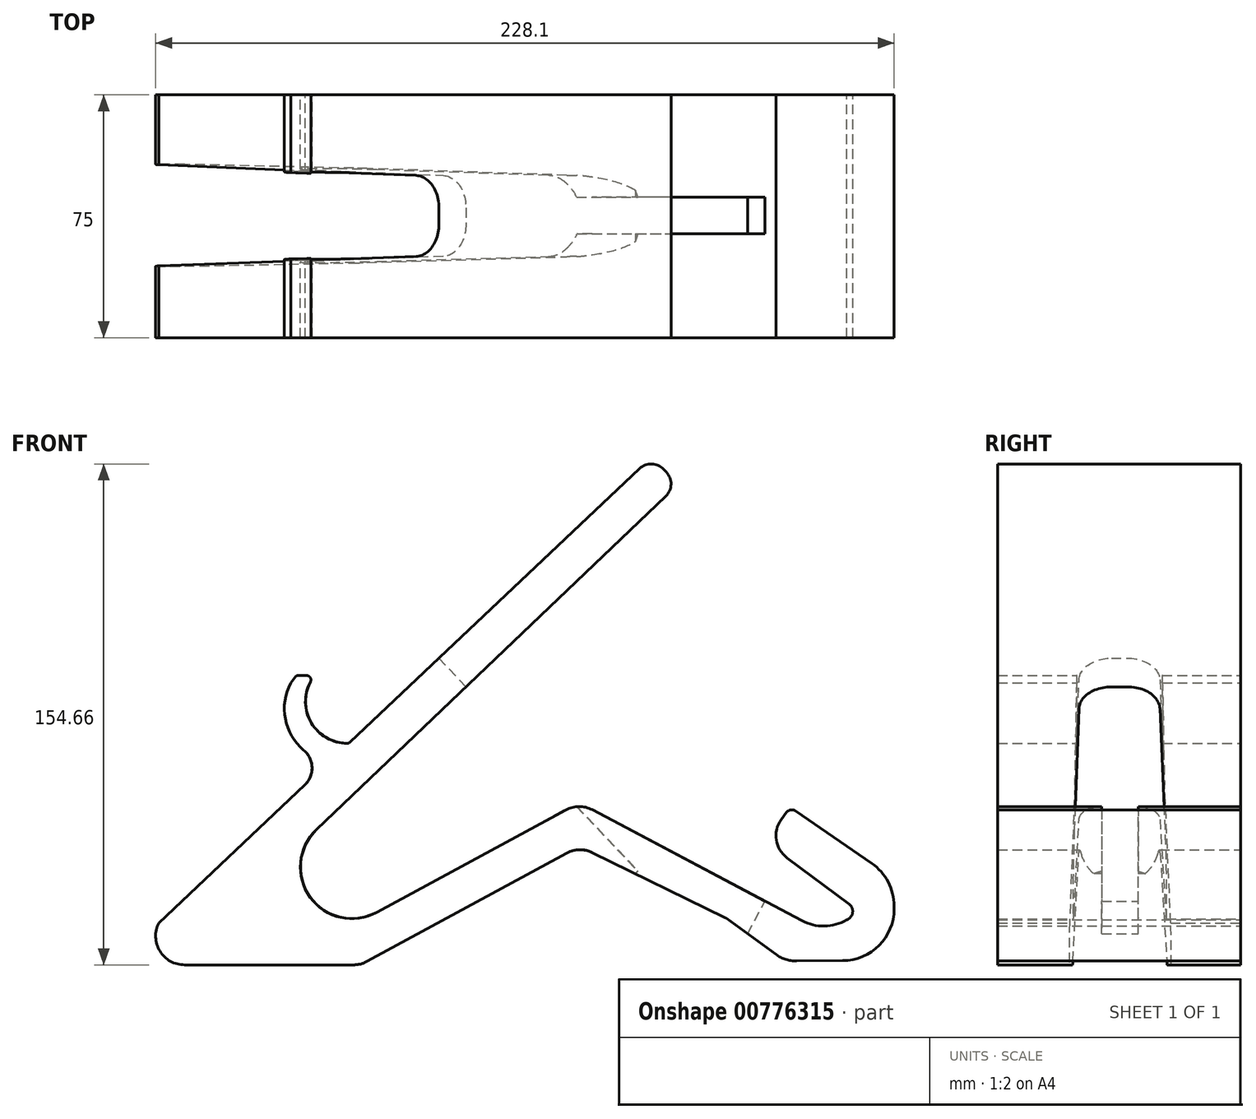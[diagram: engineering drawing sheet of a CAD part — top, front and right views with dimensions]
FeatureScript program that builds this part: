
annotation { "Feature Type Name" : "Feature", "Feature Type Description" : "" }
export const myFeature = defineFeature(function(context is Context, id is Id, definition is map)
    precondition{}
    {
        {
            var Q0;
            Q0=qCreatedBy(makeId("Front.planeOp"),FACE);
            var sketch = newSketch(context, id + "F0", { "sketchPlane" : qUnion([Q0])});
            skLineSegment(sketch, "E0", {"start": v(-57.51, -6.76) * mm, "end": v(31.9, 77.7) * mm});
            skArc(sketch, "E1", {"start": v(-116.6, -62.56) * mm, "mid": v(-116.26, -71.3) * mm, "end": v(-108.62, -75.53) * mm});
            skPoint(sketch, "E2", {"position": v(-116.6, -62.56) * mm});
            skArc(sketch, "E3", {"start": v(-75.86, 11.52) * mm, "mid": v(-77.5, 0.43) * mm, "end": v(-71.82, -9.23) * mm});
            skPoint(sketch, "E4", {"position": v(-54.93, -4.33) * mm});
            skArc(sketch, "E5", {"start": v(-69.78, 11.9) * mm, "mid": v(-69.49, -0.84) * mm, "end": v(-58.4, -7.12) * mm});
            skLineSegment(sketch, "E6", {"start": v(-70.91, 13.8) * mm, "end": v(-73.69, 13.8) * mm});
            skLineSegment(sketch, "E7", {"start": v(-74.26, 13.52) * mm, "end": v(-75.86, 11.52) * mm});
            skPoint(sketch, "E8", {"position": v(-57.87, -7.1) * mm});
            skArc(sketch, "E9.filletArc", {"start": v(-69.78, 11.9) * mm, "mid": v(-69.8, 13.17) * mm, "end": v(-70.91, 13.8) * mm});
            skArc(sketch, "E10.filletArc", {"start": v(-73.69, 13.8) * mm, "mid": v(-74, 13.73) * mm, "end": v(-74.26, 13.52) * mm});
            skArc(sketch, "E11.filletArc", {"start": v(-58.4, -7.12) * mm, "mid": v(-57.92, -7.02) * mm, "end": v(-57.51, -6.76) * mm});
            skLineSegment(sketch, "E12", {"start": v(39.99, 69.19) * mm, "end": v(-67.93, -33.77) * mm});
            skLineSegment(sketch, "E13", {"start": v(-71.52, -19.99) * mm, "end": v(-116.6, -62.56) * mm});
            skLineSegment(sketch, "E14", {"start": v(-49.28, -59.37) * mm, "end": v(9.15, -27.67) * mm});
            skLineSegment(sketch, "E15", {"start": v(17.28, -40.85) * mm, "end": v(58.34, -60.96) * mm});
            skLineSegment(sketch, "E16", {"start": v(58.65, -61.14) * mm, "end": v(74.02, -72.3) * mm});
            skArc(sketch, "E17.filletArc", {"start": v(-67.93, -33.77) * mm, "mid": v(-69.82, -54.73) * mm, "end": v(-49.28, -59.37) * mm});
            skPoint(sketch, "E18.visualSharp", {"position": v(110.3, -50.19) * mm});
            skArc(sketch, "E19.filletArc", {"start": v(-71.52, -19.99) * mm, "mid": v(-69.26, -14.54) * mm, "end": v(-71.82, -9.23) * mm});
            skLineSegment(sketch, "E20", {"start": v(84, -74.31) * mm, "end": v(94.64, -74.24) * mm});
            skLineSegment(sketch, "E21", {"start": v(110.52, -58.27) * mm, "end": v(110.52, -57.36) * mm});
            skLineSegment(sketch, "E22", {"start": v(103.6, -44.2) * mm, "end": v(80.06, -28.02) * mm});
            skArc(sketch, "E23.filletArc", {"start": v(74.02, -72.3) * mm, "mid": v(77.02, -73.82) * mm, "end": v(80.35, -74.33) * mm});
            skArc(sketch, "E24.filletArc", {"start": v(94.64, -74.24) * mm, "mid": v(105.87, -69.53) * mm, "end": v(110.52, -58.27) * mm});
            skPoint(sketch, "E25.visualSharp", {"position": v(110.52, -48.96) * mm});
            skArc(sketch, "E25.filletArc", {"start": v(110.52, -57.36) * mm, "mid": v(108.68, -49.92) * mm, "end": v(103.6, -44.2) * mm});
            skLineSegment(sketch, "E26", {"start": v(80.35, -74.33) * mm, "end": v(84, -74.31) * mm});
            skLineSegment(sketch, "E27", {"start": v(-108.62, -75.53) * mm, "end": v(-56.4, -75.53) * mm});
            skLineSegment(sketch, "E28", {"start": v(-52.3, -74.5) * mm, "end": v(9.4, -41.02) * mm});
            skPoint(sketch, "E29.visualSharp", {"position": v(-54.22, -75.53) * mm});
            skArc(sketch, "E29.filletArc", {"start": v(-56.4, -75.53) * mm, "mid": v(-54.29, -75.27) * mm, "end": v(-52.3, -74.5) * mm});
            skLineSegment(sketch, "E30", {"start": v(17.27, -27.63) * mm, "end": v(81.99, -61.9) * mm});
            skArc(sketch, "E31.filletArc", {"start": v(17.28, -40.85) * mm, "mid": v(13.32, -39.98) * mm, "end": v(9.4, -41.02) * mm});
            skArc(sketch, "E32.filletArc", {"start": v(17.27, -27.63) * mm, "mid": v(13.2, -26.63) * mm, "end": v(9.15, -27.67) * mm});
            skLineSegment(sketch, "E33", {"start": v(96.61, -56.76) * mm, "end": v(77.45, -42.5) * mm});
            skLineSegment(sketch, "E34", {"start": v(75.63, -30.68) * mm, "end": v(77.2, -28.51) * mm});
            skPoint(sketch, "E35.visualSharp", {"position": v(70.72, -37.5) * mm});
            skArc(sketch, "E35.filletArc", {"start": v(75.63, -30.68) * mm, "mid": v(74.12, -36.97) * mm, "end": v(77.45, -42.5) * mm});
            skPoint(sketch, "E36.visualSharp", {"position": v(78.38, -26.86) * mm});
            skArc(sketch, "E36.filletArc", {"start": v(80.06, -28.02) * mm, "mid": v(78.53, -27.68) * mm, "end": v(77.2, -28.51) * mm});
            skPoint(sketch, "E37.visualSharp", {"position": v(100.73, -59.83) * mm});
            skArc(sketch, "E37.filletArc", {"start": v(95.86, -61.62) * mm, "mid": v(97.7, -59.42) * mm, "end": v(96.61, -56.76) * mm});
            skPoint(sketch, "E38.visualSharp", {"position": v(82.57, -62.2) * mm});
            skArc(sketch, "E38.filletArc", {"start": v(81.99, -61.9) * mm, "mid": v(88.96, -63.56) * mm, "end": v(95.86, -61.62) * mm});
            skPoint(sketch, "E39.visualSharp", {"position": v(58.5, -61.04) * mm});
            skArc(sketch, "E39.filletArc", {"start": v(58.65, -61.14) * mm, "mid": v(58.5, -61.05) * mm, "end": v(58.34, -60.96) * mm});
            skLineSegment(sketch, "E40", {"start": v(39.34, 77.5) * mm, "end": v(40.16, 76.64) * mm});
            skPoint(sketch, "E41.visualSharp", {"position": v(35.72, 81.3) * mm});
            skArc(sketch, "E41.filletArc", {"start": v(39.34, 77.5) * mm, "mid": v(35.66, 79.13) * mm, "end": v(31.9, 77.7) * mm});
            skPoint(sketch, "E42.visualSharp", {"position": v(43.8, 72.82) * mm});
            skArc(sketch, "E42.filletArc", {"start": v(39.99, 69.19) * mm, "mid": v(41.62, 72.87) * mm, "end": v(40.16, 76.64) * mm});
            skSolve(sketch);
        }
        {
            var Q0;
            Q0=makeQuery(id+"F0.imprint","IMPRINT",FACE,{"disambiguationData":[TD([[makeQuery(id+"F0.imprint","IMPRINT",EDGE,{"derivedFrom":sQuery(id+"F0.wireOp",EDGE,"E0")}),-1.0]])]});
            extrude(context, id + "F1", {"entities" : qUnion([Q0]), "depth" : 75 * mm, "offsetDistance" : 25 * mm});
        }
        {
            var Q0;
            Q0=makeQuery(id+"F1.opExtrude","SWEPT_FACE",FACE,{"disambiguationData":[OSD([sQuery(id+"F0.wireOp",EDGE,"E0")])]});
            var sketch = newSketch(context, id + "F2", { "sketchPlane" : qUnion([Q0])});
            skLineSegment(sketch, "E43", {"start": v(-144, -21.08) * mm, "end": v(-18.39, -24.91) * mm});
            skLineSegment(sketch, "E44", {"start": v(-8.7, -34.9) * mm, "end": v(-8.7, -39.9) * mm});
            skLineSegment(sketch, "E45", {"start": v(-18.43, -49.9) * mm, "end": v(-143.46, -53.26) * mm});
            skLineSegment(sketch, "E46", {"start": v(-143.46, -53.26) * mm, "end": v(-144, -21.08) * mm});
            skPoint(sketch, "E47.visualSharp", {"position": v(-8.7, -25.2) * mm});
            skArc(sketch, "E47.filletArc", {"start": v(-8.7, -34.9) * mm, "mid": v(-11.52, -27.94) * mm, "end": v(-18.39, -24.91) * mm});
            skPoint(sketch, "E48.visualSharp", {"position": v(-8.7, -49.64) * mm});
            skArc(sketch, "E48.filletArc", {"start": v(-18.43, -49.9) * mm, "mid": v(-11.53, -46.88) * mm, "end": v(-8.7, -39.9) * mm});
            skSolve(sketch);
        }
        {
            var Q0;
            {var subQ0=sQuery(id+"F2.wireOp",EDGE,"E46");Q0=makeQuery(id+"F2.imprint","IMPRINT",FACE,{"disambiguationData":[TD([[makeQuery(id+"F2.imprint","IMPRINT",EDGE,{"derivedFrom":subQ0}),-1.0]])]});}
            var Q1;
            Q1=makeQuery(id+"F2.imprint","IMPRINT",FACE,{"disambiguationData":[TD([[makeQuery(id+"F2.imprint","IMPRINT",EDGE,{"derivedFrom":sQuery(id+"F2.wireOp",EDGE,"E44")}),-1.0]])]});
            extrude(context, id + "F3", {"entities" : qUnion([Q0, Q1]), "operationType" : NewBodyOperationType.REMOVE, "depth" : 30 * mm, "offsetDistance" : 25 * mm, "hasSecondDirection" : true, "secondDirectionOppositeDirection" : true, "secondDirectionDepth" : 90 * mm});
        }
        {
            var Q0;
            Q0=makeQuery(id+"F1.opExtrude","SWEPT_FACE",FACE,{"disambiguationData":[OSD([sQuery(id+"F0.wireOp",EDGE,"E30")])]});
            var sketch = newSketch(context, id + "F4", { "sketchPlane" : qUnion([Q0])});
            skLineSegment(sketch, "E49", {"start": v(6.45, -42.87) * mm, "end": v(88.51, -42.87) * mm});
            skLineSegment(sketch, "E50", {"start": v(88.51, -42.87) * mm, "end": v(88.51, -31.58) * mm});
            skLineSegment(sketch, "E51", {"start": v(88.51, -31.58) * mm, "end": v(6.45, -31.58) * mm});
            skLineSegment(sketch, "E52", {"start": v(3.45, -34.58) * mm, "end": v(3.45, -39.87) * mm});
            skPoint(sketch, "E53.visualSharp", {"position": v(3.45, -42.87) * mm});
            skArc(sketch, "E53.filletArc", {"start": v(3.45, -39.87) * mm, "mid": v(4.33, -41.99) * mm, "end": v(6.45, -42.87) * mm});
            skPoint(sketch, "E54.visualSharp", {"position": v(3.45, -31.58) * mm});
            skArc(sketch, "E54.filletArc", {"start": v(6.45, -31.58) * mm, "mid": v(4.33, -32.46) * mm, "end": v(3.45, -34.58) * mm});
            skSolve(sketch);
        }
        {
            var Q0;
            {var subQ0=sQuery(id+"F4.wireOp",EDGE,"E49");var subQ1=sQuery(id+"F0.wireOp",EDGE,"E30");var subQ2=makeQuery(id+"F1.opExtrude","SWEPT_EDGE",EDGE,{"disambiguationData":[OSD([subQ1,sQuery(id+"F0.wireOp",EDGE,"E32.filletArc")])]});var subQ3=makeQuery(id+"F4.imprint","INTERSECT",VERTEX,{"derivedFrom":[subQ2,subQ0]});Q0=makeQuery(id+"F4.imprint","IMPRINT",FACE,{"disambiguationData":[TD([[makeQuery(id+"F4.imprint","IMPRINT",EDGE,{"disambiguationData":[TD([[subQ3,-1.0]])],"derivedFrom":subQ0}),1.0]])]});}
            var Q1;
            Q1=makeQuery(id+"F4.imprint","IMPRINT",FACE,{"disambiguationData":[TD([[makeQuery(id+"F4.imprint","IMPRINT",EDGE,{"derivedFrom":sQuery(id+"F4.wireOp",EDGE,"E52")}),1.0]])]});
            var Q2;
            {var subQ0=sQuery(id+"F4.wireOp",EDGE,"E50");Q2=makeQuery(id+"F4.imprint","IMPRINT",FACE,{"disambiguationData":[TD([[makeQuery(id+"F4.imprint","IMPRINT",EDGE,{"derivedFrom":subQ0}),1.0]])]});}
            var Q3;
            Q3=sQuery(id+"F4.wireOp",EDGE,"E50");
            var Q4;
            Q4=sQuery(id+"F4.wireOp",EDGE,"E49");
            var Q5;
            Q5=sQuery(id+"F4.wireOp",EDGE,"E51");
            var Q6;
            Q6=sQuery(id+"F4.wireOp",EDGE,"E52");
            var Q7;
            Q7=sQuery(id+"F4.wireOp",EDGE,"E53.filletArc");
            var Q8;
            Q8=sQuery(id+"F4.wireOp",EDGE,"E54.filletArc");
            extrude(context, id + "F5", {"entities" : qUnion([Q0, Q1, Q2]), "operationType" : NewBodyOperationType.REMOVE, "surfaceEntities" : qUnion([Q3, Q4, Q5, Q6, Q7, Q8]), "oppositeDirection" : true, "depth" : 25 * mm, "offsetDistance" : 25 * mm, "hasSecondDirection" : true, "secondDirectionOppositeDirection" : false, "secondDirectionDepth" : 10 * mm});
        }
    });
